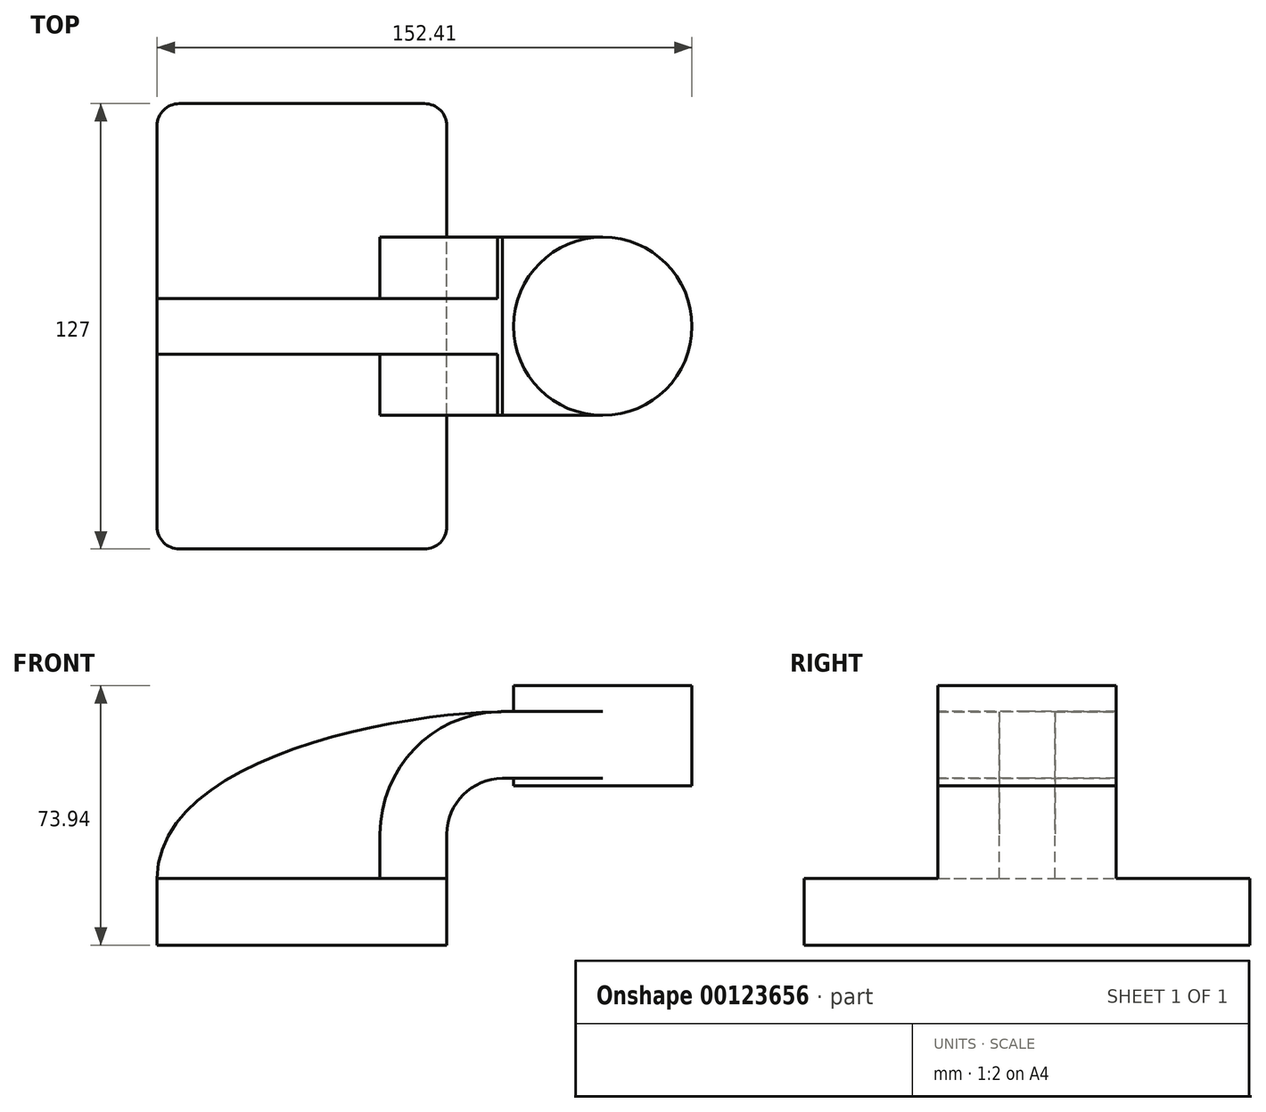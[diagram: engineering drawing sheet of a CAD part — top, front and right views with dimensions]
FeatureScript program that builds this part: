
annotation { "Feature Type Name" : "Feature", "Feature Type Description" : "" }
export const myFeature = defineFeature(function(context is Context, id is Id, definition is map)
    precondition{}
    {
        {
            var Q0;
            Q0=qCreatedBy(makeId("Front.planeOp"),FACE);
            var sketch = newSketch(context, id + "F0", { "sketchPlane" : qUnion([Q0])});
            skLineSegment(sketch, "E0.bottom", {"start": v(41.28, 9.53) * mm, "end": v(-41.28, 9.52) * mm});
            skLineSegment(sketch, "E0.top", {"start": v(41.28, -9.52) * mm, "end": v(-41.28, -9.53) * mm});
            skLineSegment(sketch, "E0.left", {"start": v(41.28, 9.53) * mm, "end": v(41.28, -9.52) * mm});
            skLineSegment(sketch, "E0.right", {"start": v(-41.28, 9.52) * mm, "end": v(-41.28, -9.53) * mm});
            skPoint(sketch, "E0.middle", {"position": v(0, 0) * mm});
            skLineSegment(sketch, "E1.bottom", {"start": v(60.32, 64.4) * mm, "end": v(111.12, 64.4) * mm});
            skLineSegment(sketch, "E1.top", {"start": v(60.32, 35.83) * mm, "end": v(111.12, 35.83) * mm});
            skLineSegment(sketch, "E1.left", {"start": v(60.32, 64.4) * mm, "end": v(60.32, 35.83) * mm});
            skLineSegment(sketch, "E1.right", {"start": v(111.12, 64.4) * mm, "end": v(111.12, 35.83) * mm});
            skPoint(sketch, "E1.middle", {"position": v(85.72, 50.12) * mm});
            skLineSegment(sketch, "E2", {"start": v(41.28, 9.53) * mm, "end": v(41.28, 22.11) * mm});
            skArc(sketch, "E3", {"start": v(41.28, 22.11) * mm, "mid": v(45.92, 33.34) * mm, "end": v(57.15, 37.99) * mm});
            skLineSegment(sketch, "E4", {"start": v(57.15, 37.99) * mm, "end": v(85.73, 37.99) * mm});
            skLineSegment(sketch, "E5.0", {"start": v(57.15, 57.04) * mm, "end": v(85.73, 57.04) * mm});
            skArc(sketch, "E5.1", {"start": v(22.23, 22.11) * mm, "mid": v(32.45, 46.8) * mm, "end": v(57.15, 57.04) * mm});
            skLineSegment(sketch, "E5.2", {"start": v(22.23, 9.53) * mm, "end": v(22.23, 22.11) * mm});
            skLineSegment(sketch, "E6", {"start": v(85.73, 37.99) * mm, "end": v(85.73, 57.04) * mm});
            skFitSpline(sketch, "E7", {"points": [v(-41.28, 9.52) * mm, v(57.15, 57.04) * mm], "startDerivative": vector(1.15, 101.71) * mm, "endDerivative": vector(96.78, 1.5) * mm});
            skLineSegment(sketch, "E8", {"start": v(85.73, 57.04) * mm, "end": v(85.72, 64.4) * mm});
            skLineSegment(sketch, "E9", {"start": v(85.72, 37.99) * mm, "end": v(85.72, 35.83) * mm});
            skSolve(sketch);
        }
        {
            var Q0;
            Q0=makeQuery(id+"F0.imprint","IMPRINT",FACE,{"disambiguationData":[TD([[makeQuery(id+"F0.imprint","IMPRINT",EDGE,{"derivedFrom":sQuery(id+"F0.wireOp",EDGE,"E0.top")}),-1.0]])]});
            extrude(context, id + "F1", {"entities" : qUnion([Q0]), "endBound" : BoundingType.SYMMETRIC, "depth" : 127 * mm});
        }
        {
            var Q0;
            {var subQ1=sQuery(id+"F0.wireOp",EDGE,"E2");Q0=makeQuery(id+"F0.imprint","IMPRINT",FACE,{"disambiguationData":[TD([[makeQuery(id+"F0.imprint","IMPRINT",EDGE,{"derivedFrom":subQ1}),1.0]])]});}
            var Q1;
            {var subQ5=sQuery(id+"F0.wireOp",EDGE,"E6");Q1=makeQuery(id+"F0.imprint","IMPRINT",FACE,{"disambiguationData":[TD([[makeQuery(id+"F0.imprint","IMPRINT",EDGE,{"derivedFrom":subQ5}),1.0]])]});}
            extrude(context, id + "F2", {"entities" : qUnion([Q0, Q1]), "operationType" : NewBodyOperationType.ADD, "endBound" : BoundingType.SYMMETRIC, "depth" : 50.8 * mm});
        }
        {
            var Q0;
            {var subQ3=sQuery(id+"F0.wireOp",EDGE,"E5.2");Q0=makeQuery(id+"F0.imprint","IMPRINT",FACE,{"disambiguationData":[TD([[makeQuery(id+"F0.imprint","IMPRINT",EDGE,{"derivedFrom":subQ3}),1.0]])]});}
            extrude(context, id + "F3", {"entities" : qUnion([Q0]), "operationType" : NewBodyOperationType.ADD, "endBound" : BoundingType.SYMMETRIC, "depth" : 15.88 * mm});
        }
        {
            var Q0;
            {var subQ0=sQuery(id+"F0.wireOp",EDGE,"E1.right");Q0=makeQuery(id+"F0.imprint","IMPRINT",FACE,{"disambiguationData":[TD([[makeQuery(id+"F0.imprint","IMPRINT",EDGE,{"derivedFrom":subQ0}),-1.0]])]});}
            var Q1;
            Q1=sQuery(id+"F0.wireOp",EDGE,"E8");
            revolve(context, id + "F4", {"operationType" : NewBodyOperationType.ADD, "entities" : qUnion([Q0]), "axis" : qUnion([Q1]), "revolveType" : RevolveType.FULL});
        }
        {
            var Q0;
            Q0=makeQuery(id+"F1.opExtrude","CAP_EDGE",EDGE,{"disambiguationData":[OSD([sQuery(id+"F0.wireOp",EDGE,"E0.left")])],"isStart":false});
            var Q1;
            Q1=makeQuery(id+"F1.opExtrude","CAP_EDGE",EDGE,{"disambiguationData":[OSD([sQuery(id+"F0.wireOp",EDGE,"E0.right")])],"isStart":false});
            var Q2;
            Q2=makeQuery(id+"F1.opExtrude","CAP_EDGE",EDGE,{"disambiguationData":[OSD([sQuery(id+"F0.wireOp",EDGE,"E0.left")])],"isStart":true});
            var Q3;
            Q3=makeQuery(id+"F1.opExtrude","CAP_EDGE",EDGE,{"disambiguationData":[OSD([sQuery(id+"F0.wireOp",EDGE,"E0.right")])],"isStart":true});
            fillet(context, id + "F5", {"entities" : qUnion([Q0, Q1, Q2, Q3]), "radius" : 6.35 * mm, "tangentPropagation" : true, "allowEdgeOverflow" : false});
        }
    });
